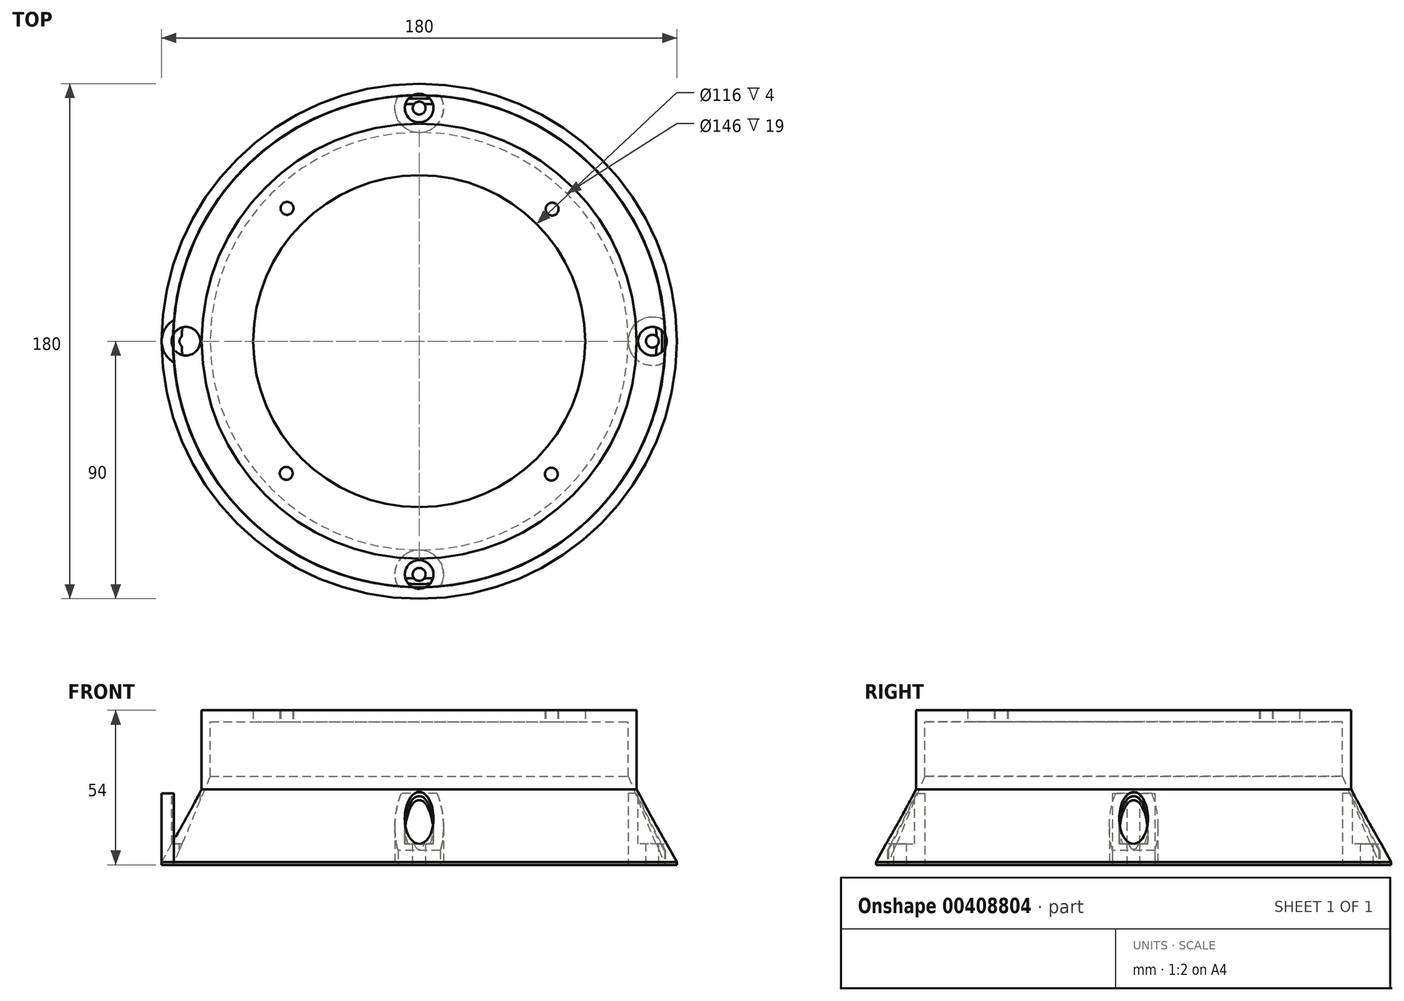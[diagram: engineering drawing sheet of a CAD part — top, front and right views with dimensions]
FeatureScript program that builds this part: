
annotation { "Feature Type Name" : "Feature", "Feature Type Description" : "" }
export const myFeature = defineFeature(function(context is Context, id is Id, definition is map)
    precondition{}
    {
        {
            var Q0;
            Q0=qCreatedBy(makeId("Top.planeOp"),FACE);
            var sketch = newSketch(context, id + "F0", { "sketchPlane" : qUnion([Q0])});
            skCircle(sketch, "E0", {"center": v(0, 0) * mm, "radius": 58 * mm});
            skCircle(sketch, "E1", {"center": v(0, 0) * mm, "radius": 61 * mm});
            skSolve(sketch);
        }
        {
            var Q0;
            Q0=makeQuery(id+"F0.imprint","IMPRINT",FACE,{"disambiguationData":[TD([[makeQuery(id+"F0.imprint","IMPRINT",EDGE,{"derivedFrom":sQuery(id+"F0.wireOp",EDGE,"E0")}),-1.0]])]});
            extrude(context, id + "F1", {"entities" : qUnion([Q0]), "depth" : 4 * mm});
        }
        {
            var Q0;
            Q0=qCreatedBy(makeId("Top.planeOp"),FACE);
            var sketch = newSketch(context, id + "F2", { "sketchPlane" : qUnion([Q0])});
            skCircle(sketch, "E2.0", {"center": v(0, 0) * mm, "radius": 56 * mm});
            skCircle(sketch, "E3.0", {"center": v(0, 0) * mm, "radius": 61 * mm});
            skSolve(sketch);
        }
        {
            var Q0;
            Q0=makeQuery(id+"F2.imprint","IMPRINT",FACE,{"disambiguationData":[TD([[makeQuery(id+"F2.imprint","IMPRINT",EDGE,{"derivedFrom":sQuery(id+"F2.wireOp",EDGE,"E2.0")}),-1.0]])]});
            extrude(context, id + "F3", {"entities" : qUnion([Q0]), "operationType" : NewBodyOperationType.ADD, "oppositeDirection" : true, "depth" : 3 * mm});
        }
        {
            var Q0;
            Q0=makeQuery(id+"F3.opExtrude","CAP_EDGE",EDGE,{"disambiguationData":[OSD([sQuery(id+"F2.wireOp",EDGE,"E2.0")])],"isStart":true});
            chamfer(context, id + "F4", {"entities" : qUnion([Q0]), "width" : 2 * mm, "tangentPropagation" : true});
        }
        {
            var Q0;
            Q0=makeQuery(id+"F3.opExtrude","CAP_FACE",FACE,{"disambiguationData":[OSD([sQuery(id+"F2.wireOp",EDGE,"E2.0"),sQuery(id+"F2.wireOp",EDGE,"E3.0")])],"isStart":false});
            var sketch = newSketch(context, id + "F5", { "sketchPlane" : qUnion([Q0])});
            skCircle(sketch, "E4", {"center": v(-46.45, 46.18) * mm, "radius": 7.5 * mm});
            skLineSegment(sketch, "E5", {"start": v(-53.95, 46.18) * mm, "end": v(-53.95, 28.46) * mm});
            skCircle(sketch, "E6", {"center": v(-46.45, 46.18) * mm, "radius": 2.25 * mm});
            skLineSegment(sketch, "E7", {"start": v(-46.57, 53.68) * mm, "end": v(-28.43, 53.97) * mm});
            skLineSegment(sketch, "E8.1.0", {"start": v(-53.68, -46.57) * mm, "end": v(-53.97, -28.43) * mm});
            skCircle(sketch, "E8.1.1", {"center": v(-46.18, -46.45) * mm, "radius": 7.5 * mm});
            skCircle(sketch, "E8.1.2", {"center": v(-46.18, -46.45) * mm, "radius": 2.25 * mm});
            skLineSegment(sketch, "E8.1.3", {"start": v(-46.18, -53.95) * mm, "end": v(-28.46, -53.95) * mm});
            skLineSegment(sketch, "E8.2.0", {"start": v(46.57, -53.68) * mm, "end": v(28.43, -53.97) * mm});
            skCircle(sketch, "E8.2.1", {"center": v(46.45, -46.18) * mm, "radius": 7.5 * mm});
            skCircle(sketch, "E8.2.2", {"center": v(46.45, -46.18) * mm, "radius": 2.25 * mm});
            skLineSegment(sketch, "E8.2.3", {"start": v(53.95, -46.18) * mm, "end": v(53.95, -28.46) * mm});
            skLineSegment(sketch, "E8.3.0", {"start": v(53.68, 46.57) * mm, "end": v(53.97, 28.43) * mm});
            skCircle(sketch, "E8.3.1", {"center": v(46.18, 46.45) * mm, "radius": 7.5 * mm});
            skCircle(sketch, "E8.3.2", {"center": v(46.18, 46.45) * mm, "radius": 2.25 * mm});
            skLineSegment(sketch, "E8.3.3", {"start": v(46.18, 53.95) * mm, "end": v(28.46, 53.95) * mm});
            skPoint(sketch, "E8.center", {"position": v(0, 0) * mm});
            skSolve(sketch);
        }
        {
            var Q0;
            Q0=qSketchRegion(id+"F5",true);
            var Q1;
            {var subQ0=sQuery(id+"F5.wireOp",EDGE,"E5");Q1=makeQuery(id+"F5.imprint","IMPRINT",FACE,{"disambiguationData":[TD([[makeQuery(id+"F5.imprint","IMPRINT",EDGE,{"derivedFrom":subQ0}),1.0]])]});}
            var Q2;
            {var subQ0=sQuery(id+"F5.wireOp",EDGE,"E7");Q2=makeQuery(id+"F5.imprint","IMPRINT",FACE,{"disambiguationData":[TD([[makeQuery(id+"F5.imprint","IMPRINT",EDGE,{"derivedFrom":subQ0}),-1.0]])]});}
            var Q3;
            {var subQ0=sQuery(id+"F5.wireOp",EDGE,"E8.3.3");Q3=makeQuery(id+"F5.imprint","IMPRINT",FACE,{"disambiguationData":[TD([[makeQuery(id+"F5.imprint","IMPRINT",EDGE,{"derivedFrom":subQ0}),1.0]])]});}
            var Q4;
            {var subQ0=sQuery(id+"F5.wireOp",EDGE,"E8.3.0");Q4=makeQuery(id+"F5.imprint","IMPRINT",FACE,{"disambiguationData":[TD([[makeQuery(id+"F5.imprint","IMPRINT",EDGE,{"derivedFrom":subQ0}),-1.0]])]});}
            var Q5;
            {var subQ0=sQuery(id+"F5.wireOp",EDGE,"E8.2.3");Q5=makeQuery(id+"F5.imprint","IMPRINT",FACE,{"disambiguationData":[TD([[makeQuery(id+"F5.imprint","IMPRINT",EDGE,{"derivedFrom":subQ0}),1.0]])]});}
            var Q6;
            {var subQ0=sQuery(id+"F5.wireOp",EDGE,"E8.2.0");Q6=makeQuery(id+"F5.imprint","IMPRINT",FACE,{"disambiguationData":[TD([[makeQuery(id+"F5.imprint","IMPRINT",EDGE,{"derivedFrom":subQ0}),-1.0]])]});}
            var Q7;
            {var subQ0=sQuery(id+"F5.wireOp",EDGE,"E8.1.3");Q7=makeQuery(id+"F5.imprint","IMPRINT",FACE,{"disambiguationData":[TD([[makeQuery(id+"F5.imprint","IMPRINT",EDGE,{"derivedFrom":subQ0}),1.0]])]});}
            var Q8;
            {var subQ0=sQuery(id+"F5.wireOp",EDGE,"E8.1.0");Q8=makeQuery(id+"F5.imprint","IMPRINT",FACE,{"disambiguationData":[TD([[makeQuery(id+"F5.imprint","IMPRINT",EDGE,{"derivedFrom":subQ0}),-1.0]])]});}
            extrude(context, id + "F6", {"entities" : qUnion([Q0, Q1, Q2, Q3, Q4, Q5, Q6, Q7, Q8]), "operationType" : NewBodyOperationType.ADD, "oppositeDirection" : true, "depth" : 7 * mm});
        }
        {
            var Q0;
            Q0=makeQuery(id+"F6.opExtrude","CAP_EDGE",EDGE,{"disambiguationData":[OSD([sQuery(id+"F5.wireOp",EDGE,"E8.3.2")])],"isStart":true});
            var Q1;
            Q1=makeQuery(id+"F6.opExtrude","CAP_EDGE",EDGE,{"disambiguationData":[OSD([sQuery(id+"F5.wireOp",EDGE,"E8.2.2")])],"isStart":true});
            var Q2;
            Q2=makeQuery(id+"F6.opExtrude","CAP_EDGE",EDGE,{"disambiguationData":[OSD([sQuery(id+"F5.wireOp",EDGE,"E8.1.2")])],"isStart":true});
            var Q3;
            Q3=makeQuery(id+"F6.opExtrude","CAP_EDGE",EDGE,{"disambiguationData":[OSD([sQuery(id+"F5.wireOp",EDGE,"E6")])],"isStart":true});
            chamfer(context, id + "F7", {"entities" : qUnion([Q0, Q1, Q2, Q3]), "width" : 3 * mm, "tangentPropagation" : true});
        }
        {
            var Q0;
            {var subQ0=sQuery(id+"F2.wireOp",EDGE,"E3.0");Q0=makeQuery(id+"F6.boolean.opBoolean","MERGE",FACE,{"derivedFrom":[makeQuery(id+"F1.opExtrude","CAP_FACE",FACE,{"disambiguationData":[OSD([sQuery(id+"F0.wireOp",EDGE,"E0"),sQuery(id+"F0.wireOp",EDGE,"E1")])],"isStart":false}),makeQuery(id+"F6.opExtrude","CAP_FACE",FACE,{"disambiguationData":[OSD([subQ0,sQuery(id+"F5.wireOp",EDGE,"E4"),sQuery(id+"F5.wireOp",EDGE,"E5"),sQuery(id+"F5.wireOp",EDGE,"E6"),sQuery(id+"F5.wireOp",EDGE,"E7")])],"isStart":false}),makeQuery(id+"F6.opExtrude","CAP_FACE",FACE,{"disambiguationData":[OSD([subQ0,sQuery(id+"F5.wireOp",EDGE,"E8.1.0"),sQuery(id+"F5.wireOp",EDGE,"E8.1.1"),sQuery(id+"F5.wireOp",EDGE,"E8.1.2"),sQuery(id+"F5.wireOp",EDGE,"E8.1.3")])],"isStart":false}),makeQuery(id+"F6.opExtrude","CAP_FACE",FACE,{"disambiguationData":[OSD([subQ0,sQuery(id+"F5.wireOp",EDGE,"E8.2.0"),sQuery(id+"F5.wireOp",EDGE,"E8.2.1"),sQuery(id+"F5.wireOp",EDGE,"E8.2.2"),sQuery(id+"F5.wireOp",EDGE,"E8.2.3")])],"isStart":false}),makeQuery(id+"F6.opExtrude","CAP_FACE",FACE,{"disambiguationData":[OSD([subQ0,sQuery(id+"F5.wireOp",EDGE,"E8.3.0"),sQuery(id+"F5.wireOp",EDGE,"E8.3.1"),sQuery(id+"F5.wireOp",EDGE,"E8.3.2"),sQuery(id+"F5.wireOp",EDGE,"E8.3.3")])],"isStart":false})]});}
            var sketch = newSketch(context, id + "F8", { "sketchPlane" : qUnion([Q0])});
            skCircle(sketch, "E9.0", {"center": v(0, 0) * mm, "radius": 56 * mm});
            skCircle(sketch, "E10.0", {"center": v(0, 0) * mm, "radius": 76 * mm});
            skCircle(sketch, "E11", {"center": v(-46.18, 46.45) * mm, "radius": 2.25 * mm});
            skCircle(sketch, "E12", {"center": v(46.45, 46.18) * mm, "radius": 2.25 * mm});
            skCircle(sketch, "E13", {"center": v(46.18, -46.45) * mm, "radius": 2.25 * mm});
            skCircle(sketch, "E14", {"center": v(-46.45, -46.18) * mm, "radius": 2.25 * mm});
            skSolve(sketch);
        }
        {
            var Q0;
            Q0=makeQuery(id+"F8.imprint","IMPRINT",FACE,{"disambiguationData":[TD([[makeQuery(id+"F8.imprint","IMPRINT",EDGE,{"derivedFrom":sQuery(id+"F8.wireOp",EDGE,"E10.0")}),1.0]])]});
            var Q1;
            Q1=makeQuery(id+"F8.imprint","IMPRINT",FACE,{"disambiguationData":[TD([[makeQuery(id+"F8.imprint","IMPRINT",EDGE,{"derivedFrom":sQuery(id+"F8.wireOp",EDGE,"E11")}),1.0]])]});
            extrude(context, id + "F9", {"entities" : qUnion([Q0, Q1]), "operationType" : NewBodyOperationType.ADD, "depth" : 4 * mm});
        }
        {
            var Q0;
            Q0=qCreatedBy(makeId("Right.planeOp"),FACE);
            var sketch = newSketch(context, id + "F10", { "sketchPlane" : qUnion([Q0])});
            skLineSegment(sketch, "E15", {"start": v(89.8, 0) * mm, "end": v(-100.67, 0) * mm});
            skLineSegment(sketch, "E16.0", {"start": v(89.8, 4) * mm, "end": v(-100.67, 4) * mm});
            skLineSegment(sketch, "E17.0", {"start": v(89.8, -3) * mm, "end": v(-100.67, -3) * mm});
            skLineSegment(sketch, "E18", {"start": v(89.8, 4) * mm, "end": v(89.8, -3) * mm});
            skLineSegment(sketch, "E19", {"start": v(-100.67, 4) * mm, "end": v(-100.67, -3) * mm});
            skSolve(sketch);
        }
        {
            var Q0;
            {var subQ0=sQuery(id+"F10.wireOp",EDGE,"E15");Q0=makeQuery(id+"F10.imprint","IMPRINT",FACE,{"disambiguationData":[TD([[makeQuery(id+"F10.imprint","IMPRINT",EDGE,{"derivedFrom":subQ0}),1.0]])]});}
            var Q1;
            {var subQ0=sQuery(id+"F10.wireOp",EDGE,"E15");Q1=makeQuery(id+"F10.imprint","IMPRINT",FACE,{"disambiguationData":[TD([[makeQuery(id+"F10.imprint","IMPRINT",EDGE,{"derivedFrom":subQ0}),-1.0]])]});}
            extrude(context, id + "F11", {"entities" : qUnion([Q0, Q1]), "operationType" : NewBodyOperationType.REMOVE, "endBound" : BoundingType.SYMMETRIC, "depth" : 200 * mm});
        }
        {
            var Q0;
            Q0=makeQuery(id+"F11.boolean.opBoolean","MERGE",FACE,{"derivedFrom":[makeQuery(id+"F9.opExtrude","CAP_FACE",FACE,{"disambiguationData":[OSD([sQuery(id+"F0.wireOp",EDGE,"E0"),sQuery(id+"F8.wireOp",EDGE,"E10.0"),sQuery(id+"F8.wireOp",EDGE,"E11"),sQuery(id+"F8.wireOp",EDGE,"E12"),sQuery(id+"F8.wireOp",EDGE,"E13"),sQuery(id+"F8.wireOp",EDGE,"E14")])],"isStart":true}),makeQuery(id+"F11.opExtrude","SWEPT_FACE",FACE,{"disambiguationData":[OSD([sQuery(id+"F10.wireOp",EDGE,"E16.0")])]})]});
            var sketch = newSketch(context, id + "F12", { "sketchPlane" : qUnion([Q0])});
            skCircle(sketch, "E20.0", {"center": v(0, 0) * mm, "radius": 73 * mm});
            skCircle(sketch, "E21.0", {"center": v(0, 0) * mm, "radius": 90 * mm});
            skCircle(sketch, "E22", {"center": v(0, 81.5) * mm, "radius": 8.5 * mm});
            skCircle(sketch, "E23", {"center": v(0, 81.5) * mm, "radius": 2.25 * mm});
            skCircle(sketch, "E24.1.0", {"center": v(-81.5, 0) * mm, "radius": 2.25 * mm});
            skCircle(sketch, "E24.1.1", {"center": v(-81.5, 0) * mm, "radius": 8.5 * mm});
            skCircle(sketch, "E24.2.0", {"center": v(0, -81.5) * mm, "radius": 2.25 * mm});
            skCircle(sketch, "E24.2.1", {"center": v(0, -81.5) * mm, "radius": 8.5 * mm});
            skCircle(sketch, "E24.3.0", {"center": v(81.5, 0) * mm, "radius": 2.25 * mm});
            skCircle(sketch, "E24.3.1", {"center": v(81.5, 0) * mm, "radius": 8.5 * mm});
            skSolve(sketch);
        }
        {
            var Q0;
            Q0=qSketchRegion(id+"F12",true);
            var Q1;
            Q1=qSketchRegion(id+"F16",true);
            extrude(context, id + "F13", {"entities" : qUnion([Q0, Q1]), "operationType" : NewBodyOperationType.ADD, "depth" : 50 * mm});
        }
        {
            var Q0;
            Q0=makeQuery(id+"F13.opExtrude","CAP_EDGE",EDGE,{"disambiguationData":[OSD([sQuery(id+"F12.wireOp",EDGE,"E21.0")])],"isStart":true});
            chamfer(context, id + "F14", {"entities" : qUnion([Q0]), "chamferType" : ChamferType.TWO_OFFSETS, "width1" : 49 * mm, "oppositeDirection" : false, "width2" : 27 * mm, "tangentPropagation" : true});
        }
        {
            var Q0;
            Q0=makeQuery(id+"F13.opExtrude","CAP_EDGE",EDGE,{"disambiguationData":[OSD([sQuery(id+"F12.wireOp",EDGE,"E20.0")])],"isStart":false});
            chamfer(context, id + "F15", {"entities" : qUnion([Q0]), "chamferType" : ChamferType.TWO_OFFSETS, "width1" : 31 * mm, "oppositeDirection" : false, "width2" : 13 * mm, "tangentPropagation" : true});
        }
        {
            var Q0;
            Q0=makeQuery(id+"F13.opExtrude","CAP_FACE",FACE,{"disambiguationData":[OSD([sQuery(id+"F12.wireOp",EDGE,"E20.0"),sQuery(id+"F12.wireOp",EDGE,"E21.0"),sQuery(id+"F12.wireOp",EDGE,"E23"),sQuery(id+"F12.wireOp",EDGE,"E24.1.0"),sQuery(id+"F12.wireOp",EDGE,"E24.2.0"),sQuery(id+"F12.wireOp",EDGE,"E24.3.0")])],"isStart":false});
            var sketch = newSketch(context, id + "F16", { "sketchPlane" : qUnion([Q0])});
            skCircle(sketch, "E25", {"center": v(-81.5, 0) * mm, "radius": 8.5 * mm});
            skCircle(sketch, "E26.1.0", {"center": v(0, -81.5) * mm, "radius": 8.5 * mm});
            skCircle(sketch, "E26.2.0", {"center": v(81.5, 0) * mm, "radius": 8.5 * mm});
            skCircle(sketch, "E26.3.0", {"center": v(0, 81.5) * mm, "radius": 8.5 * mm});
            skPoint(sketch, "E26.center", {"position": v(0, 0) * mm});
            skSolve(sketch);
        }
        {
            var Q0;
            {var subQ0=sQuery(id+"F16.wireOp",EDGE,"E25");var subQ1=sQuery(id+"F12.wireOp",EDGE,"E20.0");var subQ2=makeQuery(id+"F15.opChamfer","BLEND_EDGE",EDGE,{"blendedFrom":[makeQuery(id+"F13.opExtrude","CAP_EDGE",EDGE,{"disambiguationData":[OSD([subQ1])],"isStart":false}),makeQuery(id+"F13.opExtrude","CAP_FACE",FACE,{"disambiguationData":[OSD([subQ1,sQuery(id+"F12.wireOp",EDGE,"E21.0"),sQuery(id+"F12.wireOp",EDGE,"E23"),sQuery(id+"F12.wireOp",EDGE,"E24.1.0"),sQuery(id+"F12.wireOp",EDGE,"E24.2.0"),sQuery(id+"F12.wireOp",EDGE,"E24.3.0")])],"isStart":false})],"blendedInto":[makeQuery(id+"F13.opExtrude","CAP_FACE",FACE,{"disambiguationData":[OSD([subQ1,sQuery(id+"F12.wireOp",EDGE,"E21.0"),sQuery(id+"F12.wireOp",EDGE,"E23"),sQuery(id+"F12.wireOp",EDGE,"E24.1.0"),sQuery(id+"F12.wireOp",EDGE,"E24.2.0"),sQuery(id+"F12.wireOp",EDGE,"E24.3.0")])],"isStart":false})]});var subQ3=makeQuery(id+"F16.imprint","INTERSECT",VERTEX,{"disambiguationData":[OD(0.0)],"derivedFrom":[subQ2,subQ0]});Q0=makeQuery(id+"F16.imprint","IMPRINT",FACE,{"disambiguationData":[TD([[makeQuery(id+"F16.imprint","IMPRINT",EDGE,{"disambiguationData":[TD([[subQ3,1.0]])],"derivedFrom":subQ0}),1.0]])]});}
            var Q1;
            {var subQ0=sQuery(id+"F16.wireOp",EDGE,"E26.3.0");var subQ1=sQuery(id+"F12.wireOp",EDGE,"E20.0");var subQ2=makeQuery(id+"F15.opChamfer","BLEND_EDGE",EDGE,{"blendedFrom":[makeQuery(id+"F13.opExtrude","CAP_EDGE",EDGE,{"disambiguationData":[OSD([subQ1])],"isStart":false}),makeQuery(id+"F13.opExtrude","CAP_FACE",FACE,{"disambiguationData":[OSD([subQ1,sQuery(id+"F12.wireOp",EDGE,"E21.0"),sQuery(id+"F12.wireOp",EDGE,"E23"),sQuery(id+"F12.wireOp",EDGE,"E24.1.0"),sQuery(id+"F12.wireOp",EDGE,"E24.2.0"),sQuery(id+"F12.wireOp",EDGE,"E24.3.0")])],"isStart":false})],"blendedInto":[makeQuery(id+"F13.opExtrude","CAP_FACE",FACE,{"disambiguationData":[OSD([subQ1,sQuery(id+"F12.wireOp",EDGE,"E21.0"),sQuery(id+"F12.wireOp",EDGE,"E23"),sQuery(id+"F12.wireOp",EDGE,"E24.1.0"),sQuery(id+"F12.wireOp",EDGE,"E24.2.0"),sQuery(id+"F12.wireOp",EDGE,"E24.3.0")])],"isStart":false})]});var subQ3=makeQuery(id+"F16.imprint","INTERSECT",VERTEX,{"disambiguationData":[OD(0.0)],"derivedFrom":[subQ2,subQ0]});Q1=makeQuery(id+"F16.imprint","IMPRINT",FACE,{"disambiguationData":[TD([[makeQuery(id+"F16.imprint","IMPRINT",EDGE,{"disambiguationData":[TD([[subQ3,1.0]])],"derivedFrom":subQ0}),1.0]])]});}
            var Q2;
            {var subQ0=sQuery(id+"F16.wireOp",EDGE,"E26.2.0");var subQ1=sQuery(id+"F12.wireOp",EDGE,"E20.0");var subQ2=makeQuery(id+"F15.opChamfer","BLEND_EDGE",EDGE,{"blendedFrom":[makeQuery(id+"F13.opExtrude","CAP_EDGE",EDGE,{"disambiguationData":[OSD([subQ1])],"isStart":false}),makeQuery(id+"F13.opExtrude","CAP_FACE",FACE,{"disambiguationData":[OSD([subQ1,sQuery(id+"F12.wireOp",EDGE,"E21.0"),sQuery(id+"F12.wireOp",EDGE,"E23"),sQuery(id+"F12.wireOp",EDGE,"E24.1.0"),sQuery(id+"F12.wireOp",EDGE,"E24.2.0"),sQuery(id+"F12.wireOp",EDGE,"E24.3.0")])],"isStart":false})],"blendedInto":[makeQuery(id+"F13.opExtrude","CAP_FACE",FACE,{"disambiguationData":[OSD([subQ1,sQuery(id+"F12.wireOp",EDGE,"E21.0"),sQuery(id+"F12.wireOp",EDGE,"E23"),sQuery(id+"F12.wireOp",EDGE,"E24.1.0"),sQuery(id+"F12.wireOp",EDGE,"E24.2.0"),sQuery(id+"F12.wireOp",EDGE,"E24.3.0")])],"isStart":false})]});var subQ3=makeQuery(id+"F16.imprint","INTERSECT",VERTEX,{"disambiguationData":[OD(0.0)],"derivedFrom":[subQ2,subQ0]});Q2=makeQuery(id+"F16.imprint","IMPRINT",FACE,{"disambiguationData":[TD([[makeQuery(id+"F16.imprint","IMPRINT",EDGE,{"disambiguationData":[TD([[subQ3,1.0]])],"derivedFrom":subQ0}),1.0]])]});}
            var Q3;
            {var subQ0=sQuery(id+"F16.wireOp",EDGE,"E26.1.0");var subQ1=sQuery(id+"F12.wireOp",EDGE,"E20.0");var subQ2=makeQuery(id+"F15.opChamfer","BLEND_EDGE",EDGE,{"blendedFrom":[makeQuery(id+"F13.opExtrude","CAP_EDGE",EDGE,{"disambiguationData":[OSD([subQ1])],"isStart":false}),makeQuery(id+"F13.opExtrude","CAP_FACE",FACE,{"disambiguationData":[OSD([subQ1,sQuery(id+"F12.wireOp",EDGE,"E21.0"),sQuery(id+"F12.wireOp",EDGE,"E23"),sQuery(id+"F12.wireOp",EDGE,"E24.1.0"),sQuery(id+"F12.wireOp",EDGE,"E24.2.0"),sQuery(id+"F12.wireOp",EDGE,"E24.3.0")])],"isStart":false})],"blendedInto":[makeQuery(id+"F13.opExtrude","CAP_FACE",FACE,{"disambiguationData":[OSD([subQ1,sQuery(id+"F12.wireOp",EDGE,"E21.0"),sQuery(id+"F12.wireOp",EDGE,"E23"),sQuery(id+"F12.wireOp",EDGE,"E24.1.0"),sQuery(id+"F12.wireOp",EDGE,"E24.2.0"),sQuery(id+"F12.wireOp",EDGE,"E24.3.0")])],"isStart":false})]});var subQ3=makeQuery(id+"F16.imprint","INTERSECT",VERTEX,{"disambiguationData":[OD(0.0)],"derivedFrom":[subQ2,subQ0]});Q3=makeQuery(id+"F16.imprint","IMPRINT",FACE,{"disambiguationData":[TD([[makeQuery(id+"F16.imprint","IMPRINT",EDGE,{"disambiguationData":[TD([[subQ3,1.0]])],"derivedFrom":subQ0}),1.0]])]});}
            extrude(context, id + "F17", {"entities" : qUnion([Q0, Q1, Q2, Q3]), "oppositeDirection" : true, "depth" : 25 * mm});
        }
        {
            var Q0;
            {var subQ0=sQuery(id+"F16.wireOp",EDGE,"E26.1.0");var subQ1=sQuery(id+"F12.wireOp",EDGE,"E24.3.0");var subQ2=sQuery(id+"F12.wireOp",EDGE,"E24.2.0");var subQ3=sQuery(id+"F12.wireOp",EDGE,"E24.1.0");var subQ4=sQuery(id+"F12.wireOp",EDGE,"E23");var subQ5=sQuery(id+"F12.wireOp",EDGE,"E21.0");var subQ6=sQuery(id+"F12.wireOp",EDGE,"E20.0");var subQ7=makeQuery(id+"F15.opChamfer","BLEND_EDGE",EDGE,{"blendedFrom":[makeQuery(id+"F13.opExtrude","CAP_EDGE",EDGE,{"disambiguationData":[OSD([subQ6])],"isStart":false}),makeQuery(id+"F13.opExtrude","CAP_FACE",FACE,{"disambiguationData":[OSD([subQ6,subQ5,subQ4,subQ3,subQ2,subQ1])],"isStart":false})],"blendedInto":[makeQuery(id+"F13.opExtrude","CAP_FACE",FACE,{"disambiguationData":[OSD([subQ6,subQ5,subQ4,subQ3,subQ2,subQ1])],"isStart":false})]});Q0=makeQuery(id+"F17.opExtrude","CAP_EDGE",EDGE,{"disambiguationData":[OSD([subQ6,subQ5,subQ4,subQ3,subQ2,subQ1]),TDD([makeQuery(id+"F16.imprint","IMPRINT",EDGE,{"disambiguationData":[TD([[makeQuery(id+"F16.imprint","INTERSECT",VERTEX,{"disambiguationData":[OD(0.0)],"derivedFrom":[subQ7,subQ0]}),1.0]])],"derivedFrom":subQ7})])],"isStart":false});}
            var Q1;
            {var subQ0=sQuery(id+"F16.wireOp",EDGE,"E25");var subQ1=sQuery(id+"F12.wireOp",EDGE,"E24.3.0");var subQ2=sQuery(id+"F12.wireOp",EDGE,"E24.2.0");var subQ3=sQuery(id+"F12.wireOp",EDGE,"E24.1.0");var subQ4=sQuery(id+"F12.wireOp",EDGE,"E23");var subQ5=sQuery(id+"F12.wireOp",EDGE,"E21.0");var subQ6=sQuery(id+"F12.wireOp",EDGE,"E20.0");var subQ7=makeQuery(id+"F15.opChamfer","BLEND_EDGE",EDGE,{"blendedFrom":[makeQuery(id+"F13.opExtrude","CAP_EDGE",EDGE,{"disambiguationData":[OSD([subQ6])],"isStart":false}),makeQuery(id+"F13.opExtrude","CAP_FACE",FACE,{"disambiguationData":[OSD([subQ6,subQ5,subQ4,subQ3,subQ2,subQ1])],"isStart":false})],"blendedInto":[makeQuery(id+"F13.opExtrude","CAP_FACE",FACE,{"disambiguationData":[OSD([subQ6,subQ5,subQ4,subQ3,subQ2,subQ1])],"isStart":false})]});Q1=makeQuery(id+"F17.opExtrude","CAP_EDGE",EDGE,{"disambiguationData":[OSD([subQ6,subQ5,subQ4,subQ3,subQ2,subQ1]),TDD([makeQuery(id+"F16.imprint","IMPRINT",EDGE,{"disambiguationData":[TD([[makeQuery(id+"F16.imprint","INTERSECT",VERTEX,{"disambiguationData":[OD(0.0)],"derivedFrom":[subQ7,subQ0]}),1.0]])],"derivedFrom":subQ7})])],"isStart":false});}
            var Q2;
            {var subQ0=sQuery(id+"F16.wireOp",EDGE,"E26.3.0");var subQ1=sQuery(id+"F12.wireOp",EDGE,"E24.3.0");var subQ2=sQuery(id+"F12.wireOp",EDGE,"E24.2.0");var subQ3=sQuery(id+"F12.wireOp",EDGE,"E24.1.0");var subQ4=sQuery(id+"F12.wireOp",EDGE,"E23");var subQ5=sQuery(id+"F12.wireOp",EDGE,"E21.0");var subQ6=sQuery(id+"F12.wireOp",EDGE,"E20.0");var subQ7=makeQuery(id+"F15.opChamfer","BLEND_EDGE",EDGE,{"blendedFrom":[makeQuery(id+"F13.opExtrude","CAP_EDGE",EDGE,{"disambiguationData":[OSD([subQ6])],"isStart":false}),makeQuery(id+"F13.opExtrude","CAP_FACE",FACE,{"disambiguationData":[OSD([subQ6,subQ5,subQ4,subQ3,subQ2,subQ1])],"isStart":false})],"blendedInto":[makeQuery(id+"F13.opExtrude","CAP_FACE",FACE,{"disambiguationData":[OSD([subQ6,subQ5,subQ4,subQ3,subQ2,subQ1])],"isStart":false})]});Q2=makeQuery(id+"F17.opExtrude","CAP_EDGE",EDGE,{"disambiguationData":[OSD([subQ6,subQ5,subQ4,subQ3,subQ2,subQ1]),TDD([makeQuery(id+"F16.imprint","IMPRINT",EDGE,{"disambiguationData":[TD([[makeQuery(id+"F16.imprint","INTERSECT",VERTEX,{"disambiguationData":[OD(0.0)],"derivedFrom":[subQ7,subQ0]}),1.0]])],"derivedFrom":subQ7})])],"isStart":false});}
            var Q3;
            {var subQ0=sQuery(id+"F16.wireOp",EDGE,"E26.2.0");var subQ1=sQuery(id+"F12.wireOp",EDGE,"E24.3.0");var subQ2=sQuery(id+"F12.wireOp",EDGE,"E24.2.0");var subQ3=sQuery(id+"F12.wireOp",EDGE,"E24.1.0");var subQ4=sQuery(id+"F12.wireOp",EDGE,"E23");var subQ5=sQuery(id+"F12.wireOp",EDGE,"E21.0");var subQ6=sQuery(id+"F12.wireOp",EDGE,"E20.0");var subQ7=makeQuery(id+"F15.opChamfer","BLEND_EDGE",EDGE,{"blendedFrom":[makeQuery(id+"F13.opExtrude","CAP_EDGE",EDGE,{"disambiguationData":[OSD([subQ6])],"isStart":false}),makeQuery(id+"F13.opExtrude","CAP_FACE",FACE,{"disambiguationData":[OSD([subQ6,subQ5,subQ4,subQ3,subQ2,subQ1])],"isStart":false})],"blendedInto":[makeQuery(id+"F13.opExtrude","CAP_FACE",FACE,{"disambiguationData":[OSD([subQ6,subQ5,subQ4,subQ3,subQ2,subQ1])],"isStart":false})]});Q3=makeQuery(id+"F17.opExtrude","CAP_EDGE",EDGE,{"disambiguationData":[OSD([subQ6,subQ5,subQ4,subQ3,subQ2,subQ1]),TDD([makeQuery(id+"F16.imprint","IMPRINT",EDGE,{"disambiguationData":[TD([[makeQuery(id+"F16.imprint","INTERSECT",VERTEX,{"disambiguationData":[OD(0.0)],"derivedFrom":[subQ7,subQ0]}),1.0]])],"derivedFrom":subQ7})])],"isStart":false});}
            chamfer(context, id + "F18", {"entities" : qUnion([Q0, Q1, Q2, Q3]), "chamferType" : ChamferType.TWO_OFFSETS, "width1" : 10 * mm, "oppositeDirection" : false, "width2" : 20 * mm, "tangentPropagation" : true});
        }
        {
            var Q0;
            Q0=makeQuery(id+"F12.imprint","IMPRINT",FACE,{"disambiguationData":[TD([[makeQuery(id+"F12.imprint","IMPRINT",EDGE,{"derivedFrom":sQuery(id+"F12.wireOp",EDGE,"E24.1.0")}),1.0]])]});
            var Q1;
            Q1=makeQuery(id+"F12.imprint","IMPRINT",FACE,{"disambiguationData":[TD([[makeQuery(id+"F12.imprint","IMPRINT",EDGE,{"derivedFrom":sQuery(id+"F12.wireOp",EDGE,"E24.2.0")}),1.0]])]});
            var Q2;
            Q2=makeQuery(id+"F12.imprint","IMPRINT",FACE,{"disambiguationData":[TD([[makeQuery(id+"F12.imprint","IMPRINT",EDGE,{"derivedFrom":sQuery(id+"F12.wireOp",EDGE,"E24.3.0")}),1.0]])]});
            var Q3;
            Q3=makeQuery(id+"F12.imprint","IMPRINT",FACE,{"disambiguationData":[TD([[makeQuery(id+"F12.imprint","IMPRINT",EDGE,{"derivedFrom":sQuery(id+"F12.wireOp",EDGE,"E23")}),1.0]])]});
            extrude(context, id + "F19", {"entities" : qUnion([Q0, Q1, Q2, Q3]), "operationType" : NewBodyOperationType.REMOVE, "depth" : 73 * mm});
        }
        {
            var Q0;
            Q0=makeQuery(id+"F9.opExtrude","CAP_FACE",FACE,{"disambiguationData":[OSD([sQuery(id+"F0.wireOp",EDGE,"E0"),sQuery(id+"F8.wireOp",EDGE,"E10.0"),sQuery(id+"F8.wireOp",EDGE,"E11"),sQuery(id+"F8.wireOp",EDGE,"E12"),sQuery(id+"F8.wireOp",EDGE,"E13"),sQuery(id+"F8.wireOp",EDGE,"E14")])],"isStart":false});
            var sketch = newSketch(context, id + "F20", { "sketchPlane" : qUnion([Q0])});
            skCircle(sketch, "E27", {"center": v(0, 81.5) * mm, "radius": 5 * mm});
            skCircle(sketch, "E28.1.0", {"center": v(-81.5, 0) * mm, "radius": 5 * mm});
            skCircle(sketch, "E28.2.0", {"center": v(0, -81.5) * mm, "radius": 5 * mm});
            skCircle(sketch, "E28.3.0", {"center": v(81.5, 0) * mm, "radius": 5 * mm});
            skPoint(sketch, "E28.center", {"position": v(0, 0) * mm});
            skSolve(sketch);
        }
        {
            var Q0;
            Q0=makeQuery(id+"F20.imprint","IMPRINT",FACE,{"disambiguationData":[TD([[makeQuery(id+"F20.imprint","IMPRINT",EDGE,{"derivedFrom":sQuery(id+"F20.wireOp",EDGE,"E27")}),1.0]])]});
            var Q1;
            Q1=makeQuery(id+"F20.imprint","IMPRINT",FACE,{"disambiguationData":[TD([[makeQuery(id+"F20.imprint","IMPRINT",EDGE,{"derivedFrom":sQuery(id+"F20.wireOp",EDGE,"E28.1.0")}),1.0]])]});
            var Q2;
            Q2=makeQuery(id+"F20.imprint","IMPRINT",FACE,{"disambiguationData":[TD([[makeQuery(id+"F20.imprint","IMPRINT",EDGE,{"derivedFrom":sQuery(id+"F20.wireOp",EDGE,"E28.3.0")}),1.0]])]});
            var Q3;
            Q3=makeQuery(id+"F20.imprint","IMPRINT",FACE,{"disambiguationData":[TD([[makeQuery(id+"F20.imprint","IMPRINT",EDGE,{"derivedFrom":sQuery(id+"F20.wireOp",EDGE,"E28.2.0")}),1.0]])]});
            extrude(context, id + "F21", {"entities" : qUnion([Q0, Q1, Q2, Q3]), "operationType" : NewBodyOperationType.REMOVE, "oppositeDirection" : true, "depth" : 46.7 * mm});
        }
    });
